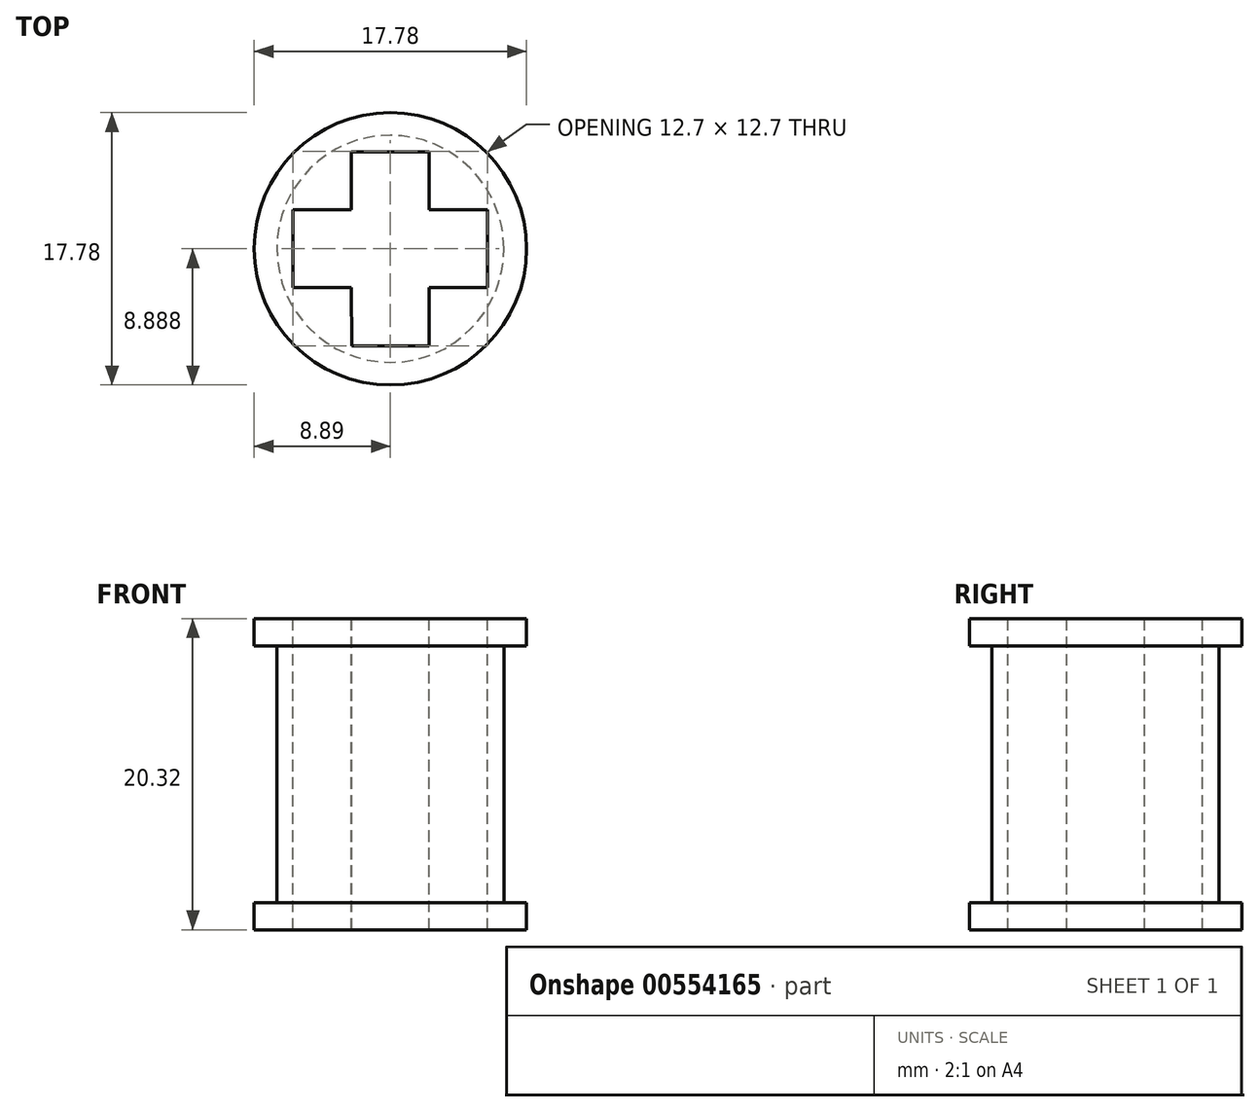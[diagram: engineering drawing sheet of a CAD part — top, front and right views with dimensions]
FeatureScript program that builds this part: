
annotation { "Feature Type Name" : "Feature", "Feature Type Description" : "" }
export const myFeature = defineFeature(function(context is Context, id is Id, definition is map)
    precondition{}
    {
        {
            var Q0;
            Q0=qCreatedBy(makeId("Top.planeOp"),FACE);
            var sketch = newSketch(context, id + "F0", { "sketchPlane" : qUnion([Q0])});
            skCircle(sketch, "E0", {"center": v(0, 0) * mm, "radius": 8.9 * mm});
            skSolve(sketch);
        }
        {
            var Q0;
            Q0 = qSketchRegion(id + "F0", true);
            extrude(context, id + "F1", {"entities" : qUnion([Q0]), "depth" : 20.32 * mm, "offsetDistance" : 25.4 * mm});
        }
        {
            var Q0;
            Q0=makeQuery(id+"F1.opExtrude","CAP_FACE",FACE,{"disambiguationData":[OSD([sQuery(id+"F0.wireOp",EDGE,"E0")])],"isStart":false});
            var sketch = newSketch(context, id + "F2", { "sketchPlane" : qUnion([Q0])});
            skLineSegment(sketch, "E1", {"start": v(0, -6.35) * mm, "end": v(2.54, -6.35) * mm});
            skLineSegment(sketch, "E2", {"start": v(0, -6.35) * mm, "end": v(-2.53, -6.35) * mm});
            skLineSegment(sketch, "E3", {"start": v(2.54, -6.35) * mm, "end": v(2.54, -2.54) * mm});
            skLineSegment(sketch, "E4", {"start": v(2.54, -2.54) * mm, "end": v(6.35, -2.54) * mm});
            skLineSegment(sketch, "E5", {"start": v(6.35, -2.54) * mm, "end": v(6.35, 0) * mm});
            skLineSegment(sketch, "E6", {"start": v(6.35, 0) * mm, "end": v(6.35, 2.54) * mm});
            skLineSegment(sketch, "E7", {"start": v(6.35, 2.54) * mm, "end": v(2.54, 2.54) * mm});
            skLineSegment(sketch, "E8", {"start": v(2.54, 2.54) * mm, "end": v(2.54, 6.35) * mm});
            skLineSegment(sketch, "E9", {"start": v(2.54, 6.35) * mm, "end": v(0, 6.35) * mm});
            skLineSegment(sketch, "E10", {"start": v(0, 6.35) * mm, "end": v(-2.54, 6.35) * mm});
            skLineSegment(sketch, "E11", {"start": v(-2.54, 6.35) * mm, "end": v(-2.54, 2.54) * mm});
            skLineSegment(sketch, "E12", {"start": v(-2.54, 2.54) * mm, "end": v(-6.35, 2.54) * mm});
            skLineSegment(sketch, "E13", {"start": v(-6.35, 2.54) * mm, "end": v(-6.35, 0) * mm});
            skLineSegment(sketch, "E14", {"start": v(-6.35, 0) * mm, "end": v(-6.35, -2.54) * mm});
            skLineSegment(sketch, "E15", {"start": v(-6.35, -2.54) * mm, "end": v(-2.54, -2.54) * mm});
            skLineSegment(sketch, "E16", {"start": v(-2.54, -2.54) * mm, "end": v(-2.53, -6.35) * mm});
            skSolve(sketch);
        }
        {
            var Q0;
            Q0=makeQuery(id+"F2.imprint","IMPRINT",FACE,{"disambiguationData":[TD([[makeQuery(id+"F2.imprint","IMPRINT",EDGE,{"derivedFrom":sQuery(id+"F2.wireOp",EDGE,"E1")}),1.0]])]});
            extrude(context, id + "F3", {"entities" : qUnion([Q0]), "operationType" : NewBodyOperationType.REMOVE, "oppositeDirection" : true, "depth" : 20.32 * mm, "offsetDistance" : 25.4 * mm});
        }
        {
            var Q0;
            Q0=qCreatedBy(makeId("Front.planeOp"),FACE);
            var sketch = newSketch(context, id + "F4", { "sketchPlane" : qUnion([Q0])});
            skLineSegment(sketch, "E17", {"start": v(11.09, 18.55) * mm, "end": v(11.09, 1.78) * mm});
            skLineSegment(sketch, "E18", {"start": v(0, 18.55) * mm, "end": v(0, 1.78) * mm});
            skLineSegment(sketch, "E19", {"start": v(11.09, 18.55) * mm, "end": v(7.4, 18.55) * mm});
            skLineSegment(sketch, "E20", {"start": v(7.4, 18.55) * mm, "end": v(7.4, 1.78) * mm});
            skLineSegment(sketch, "E21", {"start": v(7.4, 1.78) * mm, "end": v(11.09, 1.78) * mm});
            skSolve(sketch);
        }
        {
            var Q0;
            Q0 = qSketchRegion(id + "F4", true);
            var Q1;
            Q1=sQuery(id+"F4.wireOp",EDGE,"E18");
            revolve(context, id + "F5", {"operationType" : NewBodyOperationType.REMOVE, "entities" : qUnion([Q0]), "axis" : qUnion([Q1]), "revolveType" : RevolveType.FULL, "oppositeDirection" : true});
        }
    });
